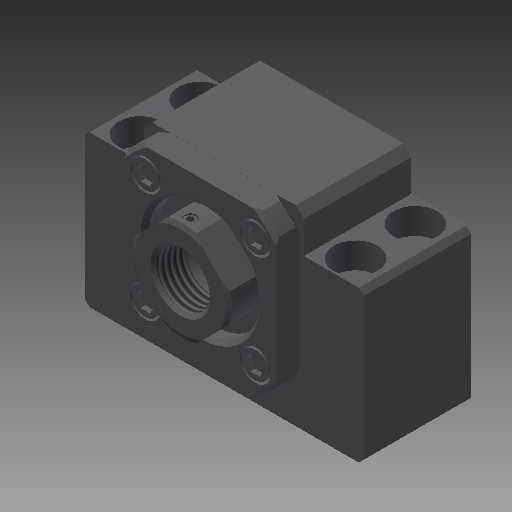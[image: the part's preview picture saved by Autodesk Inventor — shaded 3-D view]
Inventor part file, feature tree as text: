
AUTODESK INVENTOR PART (.ipt)
format: ipt  version: 2018 (Build 220112000, 112)  size: 403,456 bytes
history: native  units: mm
features: sketch x26, other x14, revolve x12, extrude x9, hole x5, pattern_linear x3, thread x1
ambient origin geometry x8: Origin, YZ Plane, XZ Plane, XY Plane, X Axis, Y Axis, Z Axis, Center Point
bodies: Solid1 (feature_tree)
feature tree (70):
  extrude  "Extrusion1"  Depth=2.5mm TaperAngle=0.0deg
  hole  "Hole1"  [1 undecoded]
  hole  "Hole2"  [1 undecoded]
  hole  "Hole3"  [1 undecoded]
  hole  "Hole4"  [1 undecoded]
  extrude  "Extrusion2"  Depth=20.0mm
  revolve  "Revolution1"  [1 undecoded]
  extrude  "Extrusion3"  Depth=20.0mm
  extrude  "Extrusion4"  TaperAngle=360.0deg  [1 undecoded]
  revolve  "Revolution2"  Angle=360.0deg
  hole  "Hole5"  [1 undecoded]
  revolve  "Revolution3"  Angle=360.0deg
  thread  "Thread1"  [1 undecoded]
  revolve  "Revolution4"  [1 undecoded]
  revolve  "Revolution5"  [1 undecoded]
  pattern_linear  "Rectangular Pattern1"  [2 undecoded]
  revolve  "Revolution6"  [1 undecoded]
  pattern_linear  "Rectangular Pattern2"  [2 undecoded]
  extrude  "Extrusion5"  [1 undecoded]
  pattern_linear  "Rectangular Pattern3"  [2 undecoded]
  revolve  "Revolution7"  [1 undecoded]
  revolve  "Revolution8"  [1 undecoded]
  extrude  "Extrusion6"  [1 undecoded]
  revolve  "Revolution9"  [1 undecoded]
  revolve  "Revolution10"  [1 undecoded]
  extrude  "Extrusion7"  [1 undecoded]
  extrude  "Extrusion8"  [1 undecoded]
  revolve  "Revolution11"  [1 undecoded]
  revolve  "Revolution12"  [1 undecoded]
  extrude  "Extrusion9"  [1 undecoded]
  other  "unit_XY"
  other  "unit_YZ"
  other  "unit_ZX"
  other  "unit_X"
  other  "unit_Y"
  other  "unit_Z"
  other  "unit_Center"
  other  "unit_collar_XY"
  other  "unit_collar_YZ"
  other  "unit_collar_ZX"
  other  "unit_collar_X"
  other  "unit_collar_Y"
  other  "unit_collar_Z"
  other  "unit_collar_Center"
  sketch  "Sketch_1"  dims[d0=27.0mm d1=0.0mm]
  sketch  "Sketch2"  dims[d2=6.6mm d3=6.0mm d4=11.0mm d5=6.5mm d6=90.0deg d7=38.0mm d8=0.0mm]
  sketch  "Sketch3"  dims[d9=6.6mm d10=6.0mm d11=11.0mm d12=6.5mm d13=90.0deg d14=38.0mm d15=0.0mm]
  sketch  "Sketch4"  dims[d16=6.6mm d17=6.0mm d18=11.0mm d19=6.5mm d20=90.0deg d21=38.0mm d22=0.0mm]
  sketch  "Sketch5"  dims[d23=6.6mm d24=6.0mm d25=11.0mm d26=6.5mm d27=90.0deg d28=38.0mm d29=0.0mm d30=2.5mm d31=0.0mm]
  sketch  "Sketch_10"  dims[d32=360.0deg d33=8.5mm d34=0.0mm]
  sketch  "Sketch_13"  dims[d49=360.0deg d50=20.0mm d52=27.577164mm d53=20.0mm d55=27.577164mm]
  sketch  "Sketch_11"  dims[d35=3.5mm d36=0.0mm d37=360.0deg]
  sketch  "Sketch_12"  dims[d46=6.876mm d47=0.0mm d48=360.0deg]
  sketch  "Sketch_14"  dims[d56=360.0deg d57=20.0mm d59=27.577164mm d60=20.0mm d62=27.577164mm]
  sketch  "Sketch11"  dims[d38=15.0mm d39=6.0mm d40=19.5mm d41=6.0mm d42=90.0deg d43=30.0mm d44=0.0mm d45=360.0deg]
  sketch  "Sketch_16"  dims[d63=1.2mm d64=0.0mm d65=20.0mm d67=27.577164mm d68=20.0mm d70=27.577164mm]
  sketch  "Sketch_17"  dims[d71=360.0deg d72=360.0deg]
  sketch  "Sketch_18"  dims[d73=1.2mm d74=0.0mm d75=360.0deg]
  sketch  "Sketch_20"  dims[d76=360.0deg d77=16.0mm d78=0.0mm]
  sketch  "Sketch_22"  dims[d79=6.0mm d80=0.0mm d81=360.0deg d82=360.0deg]
  sketch  "Sketch_24"  dims[d83=0.01mm d84=0.0mm d85=0.0mm d86=0.0mm]
  sketch  "Sketch_25"
  sketch  "Sketch_26"
  sketch  "Sketch_28"
  sketch  "Sketch_29"
  sketch  "Sketch_33"
  sketch  "Sketch_27"
  sketch  "Sketch_30"
  sketch  "Sketch_31"
  sketch  "Sketch_32"
note: 28 required parameter values undecoded (feature->parameter linkage not recoverable at this tier; creation-order binding heuristic only, values carry confidence <= 0.55)